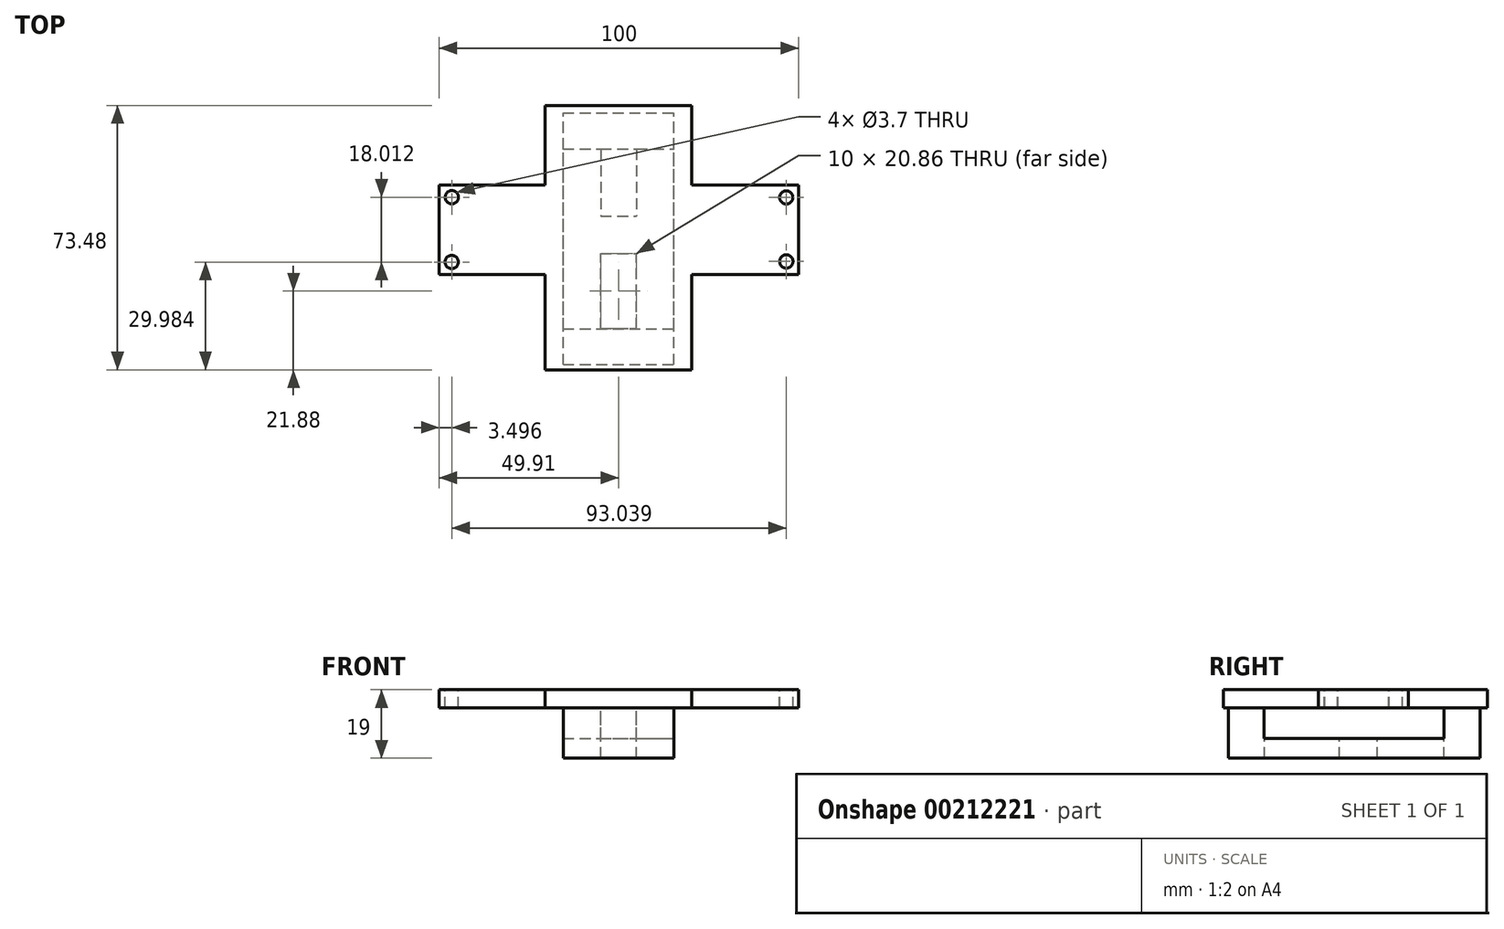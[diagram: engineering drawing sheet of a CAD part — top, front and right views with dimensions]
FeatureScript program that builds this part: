
annotation { "Feature Type Name" : "Feature", "Feature Type Description" : "" }
export const myFeature = defineFeature(function(context is Context, id is Id, definition is map)
    precondition{}
    {
        {
            var Q0;
            Q0=qCreatedBy(makeId("Top.planeOp"),FACE);
            var sketch = newSketch(context, id + "F0", { "sketchPlane" : qUnion([Q0])});
            skLineSegment(sketch, "E0.0", {"start": v(-15.4, 53.06) * mm, "end": v(-15.4, -20.42) * mm});
            skLineSegment(sketch, "E0.1", {"start": v(25.36, 53.06) * mm, "end": v(-15.4, 53.06) * mm});
            skLineSegment(sketch, "E0.2", {"start": v(25.36, -20.42) * mm, "end": v(25.36, 53.06) * mm});
            skLineSegment(sketch, "E0.3", {"start": v(-15.4, -20.42) * mm, "end": v(25.36, -20.42) * mm});
            skSolve(sketch);
        }
        {
            var Q0;
            Q0=makeQuery(id+"F0.imprint","IMPRINT",FACE,{"disambiguationData":[TD([[makeQuery(id+"F0.imprint","IMPRINT",EDGE,{"derivedFrom":sQuery(id+"F0.wireOp",EDGE,"E0.0")}),1.0]])]});
            extrude(context, id + "F1", {"entities" : qUnion([Q0]), "oppositeDirection" : true, "depth" : 5 * mm});
        }
        {
            var Q0;
            Q0=makeQuery(id+"F1.opExtrude","CAP_FACE",FACE,{"disambiguationData":[OSD([sQuery(id+"F0.wireOp",EDGE,"E0.0"),sQuery(id+"F0.wireOp",EDGE,"E0.1"),sQuery(id+"F0.wireOp",EDGE,"E0.2"),sQuery(id+"F0.wireOp",EDGE,"E0.3"),sQuery(id+"F0.wireOp",EDGE,"AwGas1L0-Tx7c-sK6K-lToC-j4NMW9GVDTDE.right")])],"isStart":false});
            var sketch = newSketch(context, id + "F2", { "sketchPlane" : qUnion([Q0])});
            skLineSegment(sketch, "E1.bottom", {"start": v(-10.4, 18.97) * mm, "end": v(20.4, 18.97) * mm});
            skLineSegment(sketch, "E1.top", {"start": v(-10.4, -51.03) * mm, "end": v(20.4, -51.03) * mm});
            skLineSegment(sketch, "E1.left", {"start": v(-10.4, 18.97) * mm, "end": v(-10.4, -51.03) * mm});
            skLineSegment(sketch, "E1.right", {"start": v(20.4, 18.97) * mm, "end": v(20.4, -51.03) * mm});
            skLineSegment(sketch, "E2", {"start": v(5, -41.03) * mm, "end": v(10, -41.03) * mm});
            skLineSegment(sketch, "E3", {"start": v(5, 8.97) * mm, "end": v(10, 8.97) * mm});
            skLineSegment(sketch, "E4", {"start": v(5, -41.03) * mm, "end": v(0, -41.03) * mm});
            skLineSegment(sketch, "E5", {"start": v(5, 8.97) * mm, "end": v(0, 8.97) * mm});
            skLineSegment(sketch, "E6", {"start": v(0, -11.89) * mm, "end": v(10, -11.89) * mm});
            skLineSegment(sketch, "E7", {"start": v(0, -22.37) * mm, "end": v(10, -22.37) * mm});
            skLineSegment(sketch, "E8", {"start": v(10, 8.97) * mm, "end": v(10, -11.89) * mm});
            skLineSegment(sketch, "E9", {"start": v(0, 8.97) * mm, "end": v(0, -11.89) * mm});
            skLineSegment(sketch, "E10", {"start": v(10, -41.03) * mm, "end": v(10, -22.37) * mm});
            skLineSegment(sketch, "E11", {"start": v(0, -41.03) * mm, "end": v(0, -22.37) * mm});
            skSolve(sketch);
        }
        {
            var Q0;
            Q0=qSketchRegion(id+"F2",true);
            extrude(context, id + "F3", {"entities" : qUnion([Q0]), "operationType" : NewBodyOperationType.ADD, "depth" : 14 * mm});
        }
        {
            var Q0;
            {var subQ0=sQuery(id+"F0.wireOp",EDGE,"AwGas1L0-Tx7c-sK6K-lToC-j4NMW9GVDTDE.right");var subQ1=sQuery(id+"F0.wireOp",EDGE,"E0.0");var subQ2=sQuery(id+"F0.wireOp",EDGE,"E0.1");var subQ3=sQuery(id+"F0.wireOp",EDGE,"E0.2");var subQ4=sQuery(id+"F0.wireOp",EDGE,"E0.3");Q0=makeQuery(id+"F3.boolean.opBoolean","SPLIT",FACE,{"disambiguationData":[TD([makeQuery(id+"F1.opExtrude","SWEPT_FACE",FACE,{"disambiguationData":[OSD([subQ2])]})])],"derivedFrom":makeQuery(id+"F1.opExtrude","CAP_FACE",FACE,{"disambiguationData":[OSD([subQ1,subQ2,subQ3,subQ4,subQ0])],"isStart":false})});}
            var sketch = newSketch(context, id + "F4", { "sketchPlane" : qUnion([Q0])});
            skLineSegment(sketch, "E12.bottom", {"start": v(-14.6, 9.01) * mm, "end": v(20.4, 9.01) * mm});
            skLineSegment(sketch, "E12.top", {"start": v(-14.6, -41) * mm, "end": v(20.4, -41) * mm});
            skLineSegment(sketch, "E12.left", {"start": v(-14.6, 9.01) * mm, "end": v(-14.6, -41) * mm});
            skLineSegment(sketch, "E12.right", {"start": v(20.4, 9.01) * mm, "end": v(20.4, -41) * mm});
            skSolve(sketch);
        }
        {
            var Q0;
            Q0=qSketchRegion(id+"F4",true);
            var Q1;
            Q1=sQuery(id+"F4.wireOp",EDGE,"E12.left");
            extrude(context, id + "F5", {"entities" : qUnion([Q0]), "operationType" : NewBodyOperationType.REMOVE, "surfaceEntities" : qUnion([Q1]), "depth" : 8.5 * mm});
        }
        {
            var Q0;
            {var subQ0=sQuery(id+"F0.wireOp",EDGE,"E0.3");var subQ1=sQuery(id+"F0.wireOp",EDGE,"E0.2");var subQ2=sQuery(id+"F0.wireOp",EDGE,"E0.1");var subQ3=sQuery(id+"F0.wireOp",EDGE,"E0.0");var subQ4=makeQuery(id+"F1.opExtrude","CAP_FACE",FACE,{"disambiguationData":[OSD([subQ3,subQ2,subQ1,subQ0])],"isStart":false});Q0=makeQuery(id+"F5.boolean.opBoolean","MERGE",FACE,{"derivedFrom":[makeQuery(id+"F3.boolean.opBoolean","SPLIT",FACE,{"disambiguationData":[TD([makeQuery(id+"F1.opExtrude","SWEPT_FACE",FACE,{"disambiguationData":[OSD([subQ3])]})])],"derivedFrom":subQ4}),makeQuery(id+"F3.boolean.opBoolean","SPLIT",FACE,{"disambiguationData":[TD([makeQuery(id+"F3.opExtrude","SWEPT_FACE",FACE,{"disambiguationData":[OSD([sQuery(id+"F2.wireOp",EDGE,"E7")])]})])],"derivedFrom":subQ4}),makeQuery(id+"F3.boolean.opBoolean","SPLIT",FACE,{"disambiguationData":[TD([makeQuery(id+"F3.opExtrude","SWEPT_FACE",FACE,{"disambiguationData":[OSD([sQuery(id+"F2.wireOp",EDGE,"E6")])]})])],"derivedFrom":subQ4}),makeQuery(id+"F5.opExtrude","CAP_FACE",FACE,{"disambiguationData":[OSD([sQuery(id+"F4.wireOp",EDGE,"E12.bottom"),sQuery(id+"F4.wireOp",EDGE,"E12.top"),sQuery(id+"F4.wireOp",EDGE,"E12.left"),sQuery(id+"F4.wireOp",EDGE,"E12.right")])],"isStart":true})]});}
            var sketch = newSketch(context, id + "F6", { "sketchPlane" : qUnion([Q0])});
            skLineSegment(sketch, "E13.bottom", {"start": v(-44.9, -31.01) * mm, "end": v(55.1, -31.01) * mm});
            skLineSegment(sketch, "E13.top", {"start": v(-44.9, -6.1) * mm, "end": v(55.1, -6.1) * mm});
            skLineSegment(sketch, "E13.left", {"start": v(-44.9, -31.01) * mm, "end": v(-44.9, -6.1) * mm});
            skLineSegment(sketch, "E13.right", {"start": v(55.1, -31.01) * mm, "end": v(55.1, -6.1) * mm});
            skPoint(sketch, "E14.endSnap0", {"position": v(4.98, -53.06) * mm});
            skSolve(sketch);
        }
        {
            var Q0;
            Q0 = qSketchRegion(id + "F6", true);
            extrude(context, id + "F7", {"entities" : qUnion([Q0]), "operationType" : NewBodyOperationType.ADD, "oppositeDirection" : true, "depth" : 5 * mm});
        }
        {
            var Q0;
            Q0=makeQuery(id+"F7.boolean.opBoolean","MERGE",FACE,{"derivedFrom":[makeQuery(id+"F1.opExtrude","CAP_FACE",FACE,{"disambiguationData":[OSD([sQuery(id+"F0.wireOp",EDGE,"E0.0"),sQuery(id+"F0.wireOp",EDGE,"E0.1"),sQuery(id+"F0.wireOp",EDGE,"E0.2"),sQuery(id+"F0.wireOp",EDGE,"E0.3")])],"isStart":true}),makeQuery(id+"F7.opExtrude","CAP_FACE",FACE,{"disambiguationData":[OSD([sQuery(id+"F6.wireOp",EDGE,"E13.bottom"),sQuery(id+"F6.wireOp",EDGE,"E13.top"),sQuery(id+"F6.wireOp",EDGE,"E13.left"),sQuery(id+"F6.wireOp",EDGE,"E13.right")])],"isStart":false})]});
            var sketch = newSketch(context, id + "F8", { "sketchPlane" : qUnion([Q0])});
            skCircle(sketch, "E15", {"center": v(-41.39, 27.58) * mm, "radius": 1.85 * mm});
            skCircle(sketch, "E16", {"center": v(51.6, 27.51) * mm, "radius": 1.85 * mm});
            skLineSegment(sketch, "E17", {"start": v(-44.9, 31.01) * mm, "end": v(-41.4, 31.01) * mm});
            skCircle(sketch, "E18", {"center": v(-41.41, 9.56) * mm, "radius": 1.85 * mm});
            skCircle(sketch, "E19", {"center": v(51.62, 9.7) * mm, "radius": 1.85 * mm});
            skSolve(sketch);
        }
        {
            var Q0;
            Q0 = qSketchRegion(id + "F8", true);
            extrude(context, id + "F9", {"entities" : qUnion([Q0]), "operationType" : NewBodyOperationType.REMOVE, "oppositeDirection" : true, "depth" : 25.4 * mm});
        }
    });
